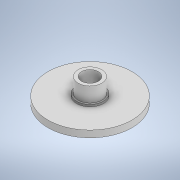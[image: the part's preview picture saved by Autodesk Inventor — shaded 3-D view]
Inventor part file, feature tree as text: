
AUTODESK INVENTOR PART (.ipt)
format: ipt  version: 2022 (Build 260153000, 153)  size: 120,832 bytes
history: native  units: mm
features: extrude x3, sketch x3
ambient origin geometry x8: Origin, YZ Plane, XZ Plane, XY Plane, X Axis, Y Axis, Z Axis, Center Point
bodies: Solid1 (feature_tree)
feature tree (6):
  extrude  "Extrusion1"  Depth=20.0mm TaperAngle=0.0deg
  extrude  "Extrusion2"  Depth=50.0mm TaperAngle=0.0deg
  extrude  "Extrusion3"  Depth=6.0mm
  sketch  "Sketch1"  dims[d0=250.0mm d1=20.0mm d2=0.0mm]
  sketch  "Sketch2"  dims[d3=50.0mm d4=50.0mm d5=0.0mm]
  sketch  "Sketch3"  dims[d6=5.0mm d7=80.0mm d8=6.0mm d9=0.0mm]
